MODEL slx_e83aa0ba6e11
CONFIG AbsTol = auto
CONFIG EnableMultiTasking = off
CONFIG FixedStep = auto
CONFIG MaxStep = auto
CONFIG MinStep = auto
CONFIG RelTol = 1e-3
CONFIG SampleTimeConstraint = Unconstrained
CONFIG Solver = VariableStepAuto
CONFIG SolverName = VariableStepAuto
CONFIG StartTime = 0.0
CONFIG StopTime = 1000
BLOCK [Constant] Constant
  Value = r
BLOCK [Demux] Demux
  DisplayOption = bar
  Outputs = 6
  Ports = [1, 6]
BLOCK [Gain] Gain
  Gain = K
  Multiplication = Matrix(K*u)
  OutDataTypeStr = Inherit: Inherit via internal rule
  ParamDataTypeStr = Inherit: Inherit via internal rule
  SaturateOnIntegerOverflow = off
BLOCK [Scope] Scope
  NumInputPorts = 3
  Ports = [3]
  ScopeSpecificationString = Simulink.scopes.TimeScopeBlockCfg('CurrentConfiguration', extmgr.ConfigurationSet(extmgr.Configuration('Core','General UI',true),extmgr.Configuration('Core','Source UI',true),extmgr.Configuration('Sources','WiredSimulink',true),extmgr.Configuration('Visuals','Time Domain',true,'SerializedDisplays',{struct('MinYLimReal','-4.23059','MaxYLimReal','22.72461','YLabelReal','','MinYLimMag','0.00000','Max...<+1379ch>
BLOCK [Scope] Scope1
  NumInputPorts = 3
  Ports = [3]
  ScopeSpecificationString = Simulink.scopes.TimeScopeBlockCfg('CurrentConfiguration', extmgr.ConfigurationSet(extmgr.Configuration('Core','General UI',true),extmgr.Configuration('Core','Source UI',true),extmgr.Configuration('Sources','WiredSimulink',true,'DataLoggingVariableName','ScopeData1','DataLoggingLimitDataPoints',true,'DataLoggingSaveFormat','Array','DataLoggingDecimation','1','DataLoggingDecimateData',true),extmgr.C...<+1532ch>
BLOCK [StateSpace] State-Space
  A = A
  B = B
  C = C
  D = D
  Ports = [1, 1]
  X0 = x0
BLOCK [Sum] Sum
  IconShape = round
  InputSameDT = off
  Inputs = |+-
  OutDataTypeStr = Inherit: Inherit via internal rule
  Ports = [2, 1]
  SaturateOnIntegerOverflow = off
LINE Constant:1 -> Sum:1
LINE Demux:1 -> Scope:1
LINE Demux:2 -> Scope:2
LINE Demux:3 -> Scope:3
LINE Demux:4 -> Scope1:1
LINE Demux:5 -> Scope1:2
LINE Demux:6 -> Scope1:3
LINE Gain:1 -> State-Space:1
LINE State-Space:1 -> Demux:1
LINE State-Space:1 -> Sum:2
LINE Sum:1 -> Gain:1
